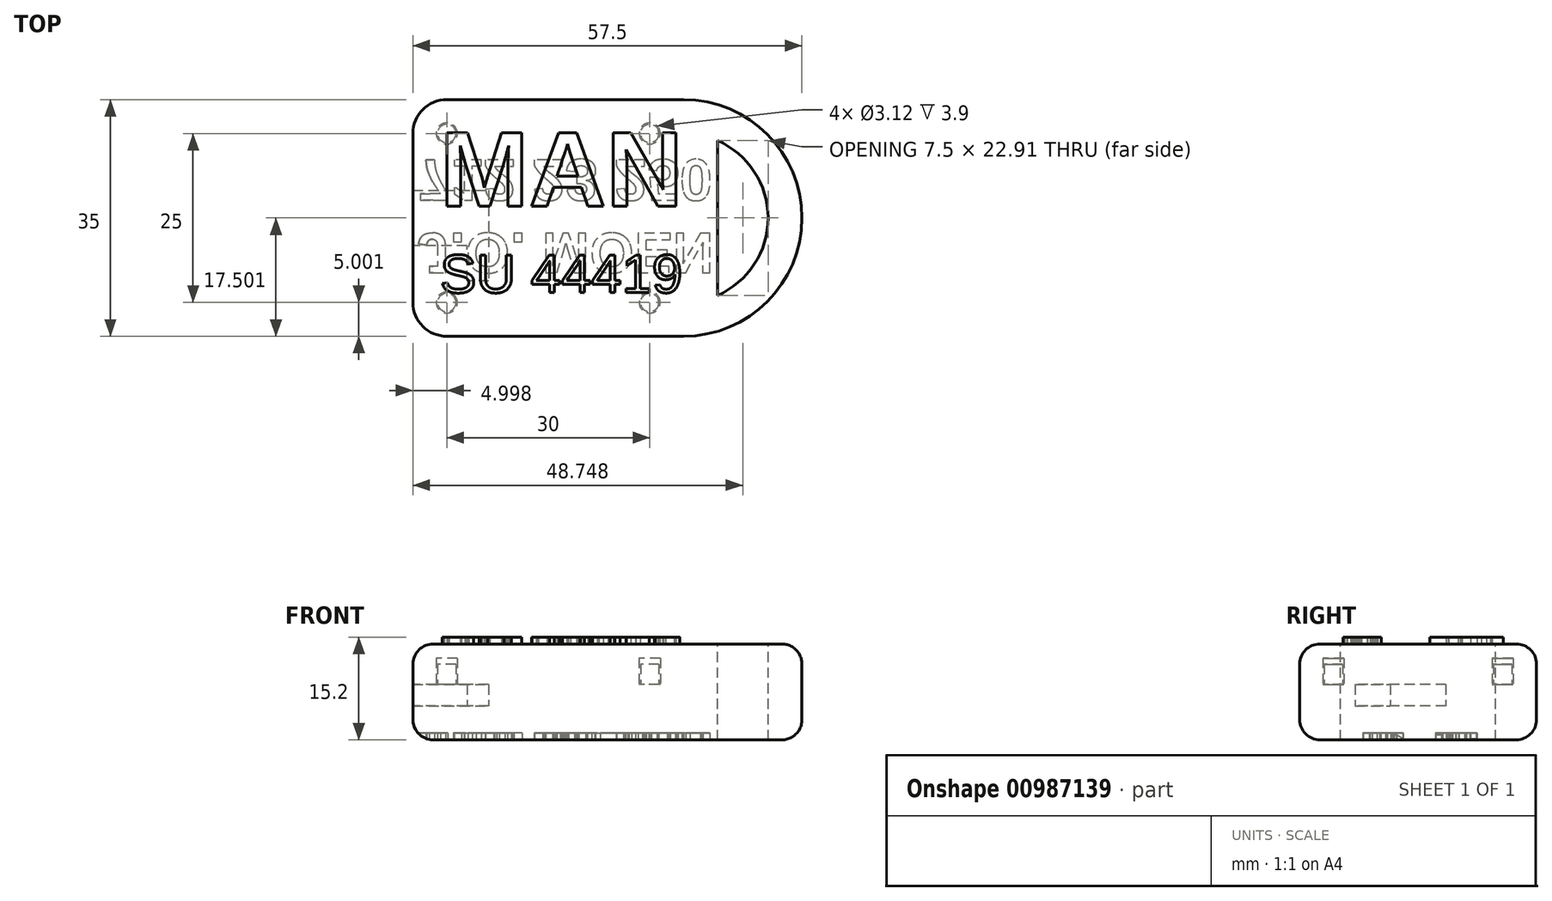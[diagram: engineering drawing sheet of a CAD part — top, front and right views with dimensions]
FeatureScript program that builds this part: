
annotation { "Feature Type Name" : "Feature", "Feature Type Description" : "" }
export const myFeature = defineFeature(function(context is Context, id is Id, definition is map)
    precondition{}
    {
        {
            var Q0;
            Q0=qCreatedBy(makeId("Top.planeOp"),FACE);
            var sketch = newSketch(context, id + "F0", { "sketchPlane" : qUnion([Q0])});
            skLineSegment(sketch, "E0.bottom", {"start": v(42.2, 28.64) * mm, "end": v(82.2, 28.64) * mm});
            skLineSegment(sketch, "E0.top", {"start": v(42.2, -6.36) * mm, "end": v(82.2, -6.36) * mm});
            skLineSegment(sketch, "E0.left", {"start": v(42.2, 28.64) * mm, "end": v(42.2, 15.24) * mm});
            skLineSegment(sketch, "E0.right", {"start": v(82.2, 28.64) * mm, "end": v(82.2, -6.36) * mm});
            skLineSegment(sketch, "E1", {"start": v(42.2, 7.04) * mm, "end": v(42.2, -6.36) * mm});
            skLineSegment(sketch, "E2", {"start": v(42.2, 15.24) * mm, "end": v(42.2, 7.04) * mm});
            skCircle(sketch, "E3", {"center": v(47.2, 23.64) * mm, "radius": 1.36 * mm});
            skLineSegment(sketch, "E4", {"start": v(47.2, 23.64) * mm, "end": v(47.2, 28.64) * mm, "construction": true});
            skLineSegment(sketch, "E5", {"start": v(47.2, 23.64) * mm, "end": v(42.2, 23.64) * mm, "construction": true});
            skCircle(sketch, "E6", {"center": v(47.2, -1.36) * mm, "radius": 1.36 * mm});
            skCircle(sketch, "E7", {"center": v(77.2, -1.36) * mm, "radius": 1.36 * mm});
            skCircle(sketch, "E8", {"center": v(77.2, 23.64) * mm, "radius": 1.36 * mm});
            skLineSegment(sketch, "E9", {"start": v(47.2, -1.36) * mm, "end": v(42.2, -1.36) * mm, "construction": true});
            skLineSegment(sketch, "E10", {"start": v(47.2, -1.36) * mm, "end": v(47.2, -6.36) * mm, "construction": true});
            skLineSegment(sketch, "E11", {"start": v(77.2, -1.36) * mm, "end": v(77.2, -6.36) * mm, "construction": true});
            skLineSegment(sketch, "E12", {"start": v(77.2, -1.36) * mm, "end": v(82.2, -1.36) * mm, "construction": true});
            skLineSegment(sketch, "E13", {"start": v(82.2, 23.64) * mm, "end": v(77.2, 23.64) * mm, "construction": true});
            skLineSegment(sketch, "E14", {"start": v(77.2, 23.64) * mm, "end": v(77.2, 28.64) * mm, "construction": true});
            skLineSegment(sketch, "E15", {"start": v(42.2, 15.24) * mm, "end": v(53.4, 15.24) * mm});
            skLineSegment(sketch, "E16", {"start": v(53.4, 15.24) * mm, "end": v(53.4, 7.04) * mm});
            skLineSegment(sketch, "E17", {"start": v(53.4, 7.04) * mm, "end": v(53.4, 1.84) * mm});
            skLineSegment(sketch, "E18", {"start": v(53.4, 1.84) * mm, "end": v(50.2, 1.84) * mm});
            skLineSegment(sketch, "E19", {"start": v(50.2, 1.84) * mm, "end": v(50.2, 7.04) * mm});
            skLineSegment(sketch, "E20", {"start": v(50.2, 7.04) * mm, "end": v(42.2, 7.04) * mm});
            skSolve(sketch);
        }
        {
            var Q0;
            {var subQ4=sQuery(id+"F0.wireOp",EDGE,"E0.bottom");Q0=makeQuery(id+"F0.imprint","IMPRINT",FACE,{"disambiguationData":[TD([[makeQuery(id+"F0.imprint","IMPRINT",EDGE,{"derivedFrom":subQ4}),-1.0]])]});}
            extrude(context, id + "F1", {"entities" : qUnion([Q0]), "depth" : 3.2 * mm, "offsetDistance" : 25 * mm});
        }
        {
            var Q0;
            {var subQ4=sQuery(id+"F0.wireOp",EDGE,"E0.bottom");Q0=makeQuery(id+"F0.imprint","IMPRINT",FACE,{"disambiguationData":[TD([[makeQuery(id+"F0.imprint","IMPRINT",EDGE,{"derivedFrom":subQ4}),-1.0]])]});}
            var Q1;
            {var subQ1=sQuery(id+"F0.wireOp",EDGE,"E2");Q1=makeQuery(id+"F0.imprint","IMPRINT",FACE,{"disambiguationData":[TD([[makeQuery(id+"F0.imprint","IMPRINT",EDGE,{"derivedFrom":subQ1}),1.0]])]});}
            var Q2;
            Q2=makeQuery(id+"F0.imprint","IMPRINT",FACE,{"disambiguationData":[TD([[makeQuery(id+"F0.imprint","IMPRINT",EDGE,{"derivedFrom":sQuery(id+"F0.wireOp",EDGE,"bb15f0e1-cc91-4aa7-aae3-7d4c7bcce2f1.0")}),1.0]])]});
            var Q3;
            Q3=makeQuery(id+"F0.imprint","IMPRINT",FACE,{"disambiguationData":[TD([[makeQuery(id+"F0.imprint","IMPRINT",EDGE,{"derivedFrom":sQuery(id+"F0.wireOp",EDGE,"E7")}),1.0]])]});
            var Q4;
            Q4=makeQuery(id+"F0.imprint","IMPRINT",FACE,{"disambiguationData":[TD([[makeQuery(id+"F0.imprint","IMPRINT",EDGE,{"derivedFrom":sQuery(id+"F0.wireOp",EDGE,"E3")}),1.0]])]});
            var Q5;
            Q5=makeQuery(id+"F0.imprint","IMPRINT",FACE,{"disambiguationData":[TD([[makeQuery(id+"F0.imprint","IMPRINT",EDGE,{"derivedFrom":sQuery(id+"F0.wireOp",EDGE,"E8")}),1.0]])]});
            var Q6;
            Q6=makeQuery(id+"F0.imprint","IMPRINT",FACE,{"disambiguationData":[TD([[makeQuery(id+"F0.imprint","IMPRINT",EDGE,{"derivedFrom":sQuery(id+"F0.wireOp",EDGE,"E6")}),1.0]])]});
            extrude(context, id + "F2", {"entities" : qUnion([Q0, Q1, Q2, Q3, Q4, Q5, Q6]), "operationType" : NewBodyOperationType.ADD, "oppositeDirection" : true, "depth" : 5 * mm, "offsetDistance" : 25 * mm});
        }
        {
            var Q0;
            Q0=makeQuery(id+"F0.imprint","IMPRINT",FACE,{"disambiguationData":[TD([[makeQuery(id+"F0.imprint","IMPRINT",EDGE,{"derivedFrom":sQuery(id+"F0.wireOp",EDGE,"E6")}),1.0]])]});
            var Q1;
            Q1=makeQuery(id+"F0.imprint","IMPRINT",FACE,{"disambiguationData":[TD([[makeQuery(id+"F0.imprint","IMPRINT",EDGE,{"derivedFrom":sQuery(id+"F0.wireOp",EDGE,"E7")}),1.0]])]});
            var Q2;
            Q2=makeQuery(id+"F0.imprint","IMPRINT",FACE,{"disambiguationData":[TD([[makeQuery(id+"F0.imprint","IMPRINT",EDGE,{"derivedFrom":sQuery(id+"F0.wireOp",EDGE,"E8")}),1.0]])]});
            var Q3;
            Q3=makeQuery(id+"F0.imprint","IMPRINT",FACE,{"disambiguationData":[TD([[makeQuery(id+"F0.imprint","IMPRINT",EDGE,{"derivedFrom":sQuery(id+"F0.wireOp",EDGE,"E3")}),1.0]])]});
            var Q4;
            Q4=makeQuery(id+"F1.opExtrude","CAP_FACE",FACE,{"disambiguationData":[OSD([sQuery(id+"F0.wireOp",EDGE,"E0.bottom"),sQuery(id+"F0.wireOp",EDGE,"E0.top"),sQuery(id+"F0.wireOp",EDGE,"E0.left"),sQuery(id+"F0.wireOp",EDGE,"E0.right"),sQuery(id+"F0.wireOp",EDGE,"E1"),sQuery(id+"F0.wireOp",EDGE,"fb78b1c1-1042-4b1b-a41c-8e915558833c.0"),sQuery(id+"F0.wireOp",EDGE,"fb78b1c1-1042-4b1b-a41c-8e915558833c.1"),sQuery(id+"F0.wireOp",EDGE,"fb78b1c1-1042-4b1b-a41c-8e915558833c.2"),sQuery(id+"F0.wireOp",EDGE,"fb78b1c1-1042-4b1b-a41c-8e915558833c.3"),sQuery(id+"F0.wireOp",EDGE,"fb78b1c1-1042-4b1b-a41c-8e915558833c.4"),sQuery(id+"F0.wireOp",EDGE,"fb78b1c1-1042-4b1b-a41c-8e915558833c.5"),sQuery(id+"F0.wireOp",EDGE,"fb78b1c1-1042-4b1b-a41c-8e915558833c.6"),sQuery(id+"F0.wireOp",EDGE,"fb78b1c1-1042-4b1b-a41c-8e915558833c.7"),sQuery(id+"F0.wireOp",EDGE,"fb78b1c1-1042-4b1b-a41c-8e915558833c.8"),sQuery(id+"F0.wireOp",EDGE,"fb78b1c1-1042-4b1b-a41c-8e915558833c.9"),sQuery(id+"F0.wireOp",EDGE,"fb78b1c1-1042-4b1b-a41c-8e915558833c.10"),sQuery(id+"F0.wireOp",EDGE,"E3"),sQuery(id+"F0.wireOp",EDGE,"E6"),sQuery(id+"F0.wireOp",EDGE,"E7"),sQuery(id+"F0.wireOp",EDGE,"E8")])],"isStart":false});
            extrude(context, id + "F3", {"entities" : qUnion([Q0, Q1, Q2, Q3]), "operationType" : NewBodyOperationType.ADD, "endBound" : BoundingType.UP_TO_SURFACE, "depth" : 5 * mm, "endBoundEntityFace" : qUnion([Q4]), "hasOffset" : true, "offsetDistance" : 3 * mm, "offsetOppositeDirection" : true});
        }
        {
            var Q0;
            Q0=makeQuery(id+"F1.opExtrude","CAP_FACE",FACE,{"disambiguationData":[OSD([sQuery(id+"F0.wireOp",EDGE,"E0.bottom"),sQuery(id+"F0.wireOp",EDGE,"E0.top"),sQuery(id+"F0.wireOp",EDGE,"E0.left"),sQuery(id+"F0.wireOp",EDGE,"E0.right"),sQuery(id+"F0.wireOp",EDGE,"E1"),sQuery(id+"F0.wireOp",EDGE,"fb78b1c1-1042-4b1b-a41c-8e915558833c.0"),sQuery(id+"F0.wireOp",EDGE,"fb78b1c1-1042-4b1b-a41c-8e915558833c.1"),sQuery(id+"F0.wireOp",EDGE,"fb78b1c1-1042-4b1b-a41c-8e915558833c.2"),sQuery(id+"F0.wireOp",EDGE,"fb78b1c1-1042-4b1b-a41c-8e915558833c.3"),sQuery(id+"F0.wireOp",EDGE,"fb78b1c1-1042-4b1b-a41c-8e915558833c.4"),sQuery(id+"F0.wireOp",EDGE,"fb78b1c1-1042-4b1b-a41c-8e915558833c.5"),sQuery(id+"F0.wireOp",EDGE,"fb78b1c1-1042-4b1b-a41c-8e915558833c.6"),sQuery(id+"F0.wireOp",EDGE,"fb78b1c1-1042-4b1b-a41c-8e915558833c.7"),sQuery(id+"F0.wireOp",EDGE,"fb78b1c1-1042-4b1b-a41c-8e915558833c.8"),sQuery(id+"F0.wireOp",EDGE,"fb78b1c1-1042-4b1b-a41c-8e915558833c.9"),sQuery(id+"F0.wireOp",EDGE,"fb78b1c1-1042-4b1b-a41c-8e915558833c.10"),sQuery(id+"F0.wireOp",EDGE,"E3"),sQuery(id+"F0.wireOp",EDGE,"E6"),sQuery(id+"F0.wireOp",EDGE,"E7"),sQuery(id+"F0.wireOp",EDGE,"E8")])],"isStart":false});
            var sketch = newSketch(context, id + "F4", { "sketchPlane" : qUnion([Q0])});
            skLineSegment(sketch, "E21.bottom", {"start": v(42.2, 28.64) * mm, "end": v(82.2, 28.64) * mm});
            skLineSegment(sketch, "E21.top", {"start": v(42.2, -6.36) * mm, "end": v(82.2, -6.36) * mm});
            skLineSegment(sketch, "E21.left", {"start": v(42.2, 28.64) * mm, "end": v(42.2, -6.36) * mm});
            skLineSegment(sketch, "E21.right", {"start": v(82.2, 28.64) * mm, "end": v(82.2, -6.36) * mm});
            skCircle(sketch, "E22", {"center": v(47.2, 23.64) * mm, "radius": 1.56 * mm});
            skCircle(sketch, "E23", {"center": v(77.2, 23.64) * mm, "radius": 1.56 * mm});
            skCircle(sketch, "E24", {"center": v(77.2, -1.36) * mm, "radius": 1.56 * mm});
            skCircle(sketch, "E25", {"center": v(47.2, -1.36) * mm, "radius": 1.56 * mm});
            skSolve(sketch);
        }
        {
            var Q0;
            {var subQ1=sQuery(id+"F4.wireOp",EDGE,"E21.bottom");Q0=makeQuery(id+"F4.imprint","IMPRINT",FACE,{"disambiguationData":[TD([[makeQuery(id+"F4.imprint","IMPRINT",EDGE,{"derivedFrom":subQ1}),-1.0]])]});}
            var Q1;
            {var subQ2=makeQuery(id+"F1.opExtrude","CAP_EDGE",EDGE,{"disambiguationData":[OSD([sQuery(id+"F0.wireOp",EDGE,"fb78b1c1-1042-4b1b-a41c-8e915558833c.0")])],"isStart":false});Q1=makeQuery(id+"F4.imprint","IMPRINT",FACE,{"disambiguationData":[TD([[makeQuery(id+"F4.imprint","IMPRINT",EDGE,{"derivedFrom":subQ2}),-1.0]])]});}
            var Q2;
            {var subQ0=makeQuery(id+"F1.opExtrude","CAP_EDGE",EDGE,{"disambiguationData":[OSD([sQuery(id+"F0.wireOp",EDGE,"E15")])],"isStart":false});Q2=makeQuery(id+"F4.imprint","IMPRINT",FACE,{"disambiguationData":[TD([[makeQuery(id+"F4.imprint","IMPRINT",EDGE,{"derivedFrom":subQ0}),-1.0]])]});}
            var Q3;
            Q3=makeQuery(id+"F3.opExtrude","CAP_FACE",FACE,{"disambiguationData":[OSD([sQuery(id+"F0.wireOp",EDGE,"E3")])],"isStart":false});
            extrude(context, id + "F5", {"entities" : qUnion([Q0, Q1, Q2]), "endBound" : BoundingType.UP_TO_SURFACE, "depth" : 25 * mm, "endBoundEntityFace" : qUnion([Q3]), "hasOffset" : true, "offsetDistance" : 1 * mm, "offsetOppositeDirection" : true});
        }
        {
            var Q0;
            Q0=makeQuery(id+"F5.opExtrude","CAP_FACE",FACE,{"disambiguationData":[OSD([sQuery(id+"F4.wireOp",EDGE,"E21.bottom"),sQuery(id+"F4.wireOp",EDGE,"E21.top"),sQuery(id+"F4.wireOp",EDGE,"E21.left"),sQuery(id+"F4.wireOp",EDGE,"E21.right"),sQuery(id+"F4.wireOp",EDGE,"E22"),sQuery(id+"F4.wireOp",EDGE,"E23"),sQuery(id+"F4.wireOp",EDGE,"E24"),sQuery(id+"F4.wireOp",EDGE,"E25")])],"isStart":false});
            var sketch = newSketch(context, id + "F6", { "sketchPlane" : qUnion([Q0])});
            skLineSegment(sketch, "E26.bottom", {"start": v(42.2, 28.64) * mm, "end": v(82.2, 28.64) * mm});
            skLineSegment(sketch, "E26.top", {"start": v(42.2, -6.36) * mm, "end": v(82.2, -6.36) * mm});
            skLineSegment(sketch, "E26.left", {"start": v(42.2, 28.64) * mm, "end": v(42.2, -6.36) * mm});
            skLineSegment(sketch, "E26.right", {"start": v(82.2, 28.64) * mm, "end": v(82.2, -6.36) * mm});
            skSolve(sketch);
        }
        {
            var Q0;
            Q0=makeQuery(id+"F6.imprint","IMPRINT",FACE,{"disambiguationData":[TD([[makeQuery(id+"F6.imprint","IMPRINT",EDGE,{"derivedFrom":makeQuery(id+"F5.opExtrude","CAP_EDGE",EDGE,{"disambiguationData":[OSD([sQuery(id+"F4.wireOp",EDGE,"E22")])],"isStart":false})}),1.0]])]});
            var Q1;
            Q1=makeQuery(id+"F6.imprint","IMPRINT",FACE,{"disambiguationData":[TD([[makeQuery(id+"F6.imprint","IMPRINT",EDGE,{"derivedFrom":makeQuery(id+"F5.opExtrude","CAP_EDGE",EDGE,{"disambiguationData":[OSD([sQuery(id+"F4.wireOp",EDGE,"E24")])],"isStart":false})}),1.0]])]});
            var Q2;
            Q2=makeQuery(id+"F6.imprint","IMPRINT",FACE,{"disambiguationData":[TD([[makeQuery(id+"F6.imprint","IMPRINT",EDGE,{"derivedFrom":makeQuery(id+"F5.opExtrude","CAP_EDGE",EDGE,{"disambiguationData":[OSD([sQuery(id+"F4.wireOp",EDGE,"E23")])],"isStart":false})}),1.0]])]});
            var Q3;
            Q3=makeQuery(id+"F6.imprint","IMPRINT",FACE,{"disambiguationData":[TD([[makeQuery(id+"F6.imprint","IMPRINT",EDGE,{"derivedFrom":makeQuery(id+"F5.opExtrude","CAP_EDGE",EDGE,{"disambiguationData":[OSD([sQuery(id+"F4.wireOp",EDGE,"E25")])],"isStart":false})}),1.0]])]});
            var Q4;
            Q4=makeQuery(id+"F3.opExtrude","CAP_FACE",FACE,{"disambiguationData":[OSD([sQuery(id+"F0.wireOp",EDGE,"E6")])],"isStart":false});
            extrude(context, id + "F7", {"entities" : qUnion([Q0, Q1, Q2, Q3]), "operationType" : NewBodyOperationType.ADD, "endBound" : BoundingType.UP_TO_SURFACE, "oppositeDirection" : true, "depth" : 25 * mm, "endBoundEntityFace" : qUnion([Q4]), "hasOffset" : true, "offsetDistance" : 0.9 * mm});
        }
        {
            var Q0;
            {var subQ0=sQuery(id+"F4.wireOp",EDGE,"E25");var subQ1=sQuery(id+"F4.wireOp",EDGE,"E24");var subQ2=sQuery(id+"F4.wireOp",EDGE,"E23");var subQ3=sQuery(id+"F4.wireOp",EDGE,"E22");Q0=makeQuery(id+"F7.boolean.opBoolean","MERGE",FACE,{"derivedFrom":[makeQuery(id+"F5.opExtrude","CAP_FACE",FACE,{"disambiguationData":[OSD([sQuery(id+"F4.wireOp",EDGE,"E21.bottom"),sQuery(id+"F4.wireOp",EDGE,"E21.top"),sQuery(id+"F4.wireOp",EDGE,"E21.left"),sQuery(id+"F4.wireOp",EDGE,"E21.right"),subQ3,subQ2,subQ1,subQ0])],"isStart":false}),makeQuery(id+"F7.opExtrude","CAP_FACE",FACE,{"disambiguationData":[OSD([subQ3])],"isStart":true}),makeQuery(id+"F7.opExtrude","CAP_FACE",FACE,{"disambiguationData":[OSD([subQ2])],"isStart":true}),makeQuery(id+"F7.opExtrude","CAP_FACE",FACE,{"disambiguationData":[OSD([subQ1])],"isStart":true}),makeQuery(id+"F7.opExtrude","CAP_FACE",FACE,{"disambiguationData":[OSD([subQ0])],"isStart":true})]});}
            var sketch = newSketch(context, id + "F8", { "sketchPlane" : qUnion([Q0])});
            skSolve(sketch);
        }
        {
            var Q0;
            Q0=makeQuery(id+"F8.imprint","IMPRINT",FACE,{"disambiguationData":[TD([[makeQuery(id+"F8.imprint","IMPRINT",EDGE,{"derivedFrom":makeQuery(id+"F5.opExtrude","CAP_EDGE",EDGE,{"disambiguationData":[OSD([sQuery(id+"F4.wireOp",EDGE,"E21.bottom")])],"isStart":false})}),-1.0]])]});
            extrude(context, id + "F9", {"entities" : qUnion([Q0]), "operationType" : NewBodyOperationType.ADD, "depth" : 2 * mm, "offsetDistance" : 25 * mm});
        }
        {
            var Q0;
            Q0=makeQuery(id+"F9.opExtrude","CAP_FACE",FACE,{"disambiguationData":[OSD([sQuery(id+"F4.wireOp",EDGE,"E21.bottom"),sQuery(id+"F4.wireOp",EDGE,"E21.top"),sQuery(id+"F4.wireOp",EDGE,"E21.left"),sQuery(id+"F4.wireOp",EDGE,"E21.right")])],"isStart":false});
            var sketch = newSketch(context, id + "F10", { "sketchPlane" : qUnion([Q0])});
            skText(sketch, "E27", { "text": "MAN", "fontName": "Arimo-Bold.ttf"});
            skText(sketch, "E28", { "text": "SU 44419", "fontName": "Arimo-Regular.ttf"});
            const initialGuessF10  = {"E27": [0.0462, 0.01287, 1, 0, 0.01137], "E28": [0.0462, 0.0001, 1, 0, 0.0058]};
            skSetInitialGuess(sketch, initialGuessF10);
            skSolve(sketch);
        }
        {
            var Q0;
            Q0 = qSketchRegion(id + "F10", true);
            extrude(context, id + "F11", {"entities" : qUnion([Q0]), "operationType" : NewBodyOperationType.ADD, "depth" : 1 * mm, "offsetDistance" : 25 * mm});
        }
        {
            var Q0;
            {var subQ0=sQuery(id+"F0.wireOp",EDGE,"E0.left");var subQ1=sQuery(id+"F0.wireOp",EDGE,"E0.bottom");Q0=makeQuery(id+"F2.boolean.opBoolean","MERGE",EDGE,{"derivedFrom":[makeQuery(id+"F1.opExtrude","SWEPT_EDGE",EDGE,{"disambiguationData":[OSD([subQ1,subQ0])]}),makeQuery(id+"F2.opExtrude","SWEPT_EDGE",EDGE,{"disambiguationData":[OSD([subQ1,subQ0])]})]});}
            var Q1;
            {var subQ0=sQuery(id+"F4.wireOp",EDGE,"E21.left");var subQ1=sQuery(id+"F4.wireOp",EDGE,"E21.bottom");Q1=makeQuery(id+"F9.boolean.opBoolean","MERGE",EDGE,{"derivedFrom":[makeQuery(id+"F5.opExtrude","SWEPT_EDGE",EDGE,{"disambiguationData":[OSD([subQ1,subQ0])]}),makeQuery(id+"F9.opExtrude","SWEPT_EDGE",EDGE,{"disambiguationData":[OSD([subQ1,subQ0])]})]});}
            var Q2;
            {var subQ0=sQuery(id+"F0.wireOp",EDGE,"E1");var subQ1=sQuery(id+"F0.wireOp",EDGE,"E0.top");Q2=makeQuery(id+"F2.boolean.opBoolean","MERGE",EDGE,{"derivedFrom":[makeQuery(id+"F1.opExtrude","SWEPT_EDGE",EDGE,{"disambiguationData":[OSD([subQ1,subQ0])]}),makeQuery(id+"F2.opExtrude","SWEPT_EDGE",EDGE,{"disambiguationData":[OSD([subQ1,subQ0])]})]});}
            var Q3;
            {var subQ0=sQuery(id+"F4.wireOp",EDGE,"E21.left");var subQ1=sQuery(id+"F4.wireOp",EDGE,"E21.top");Q3=makeQuery(id+"F9.boolean.opBoolean","MERGE",EDGE,{"derivedFrom":[makeQuery(id+"F5.opExtrude","SWEPT_EDGE",EDGE,{"disambiguationData":[OSD([subQ1,subQ0])]}),makeQuery(id+"F9.opExtrude","SWEPT_EDGE",EDGE,{"disambiguationData":[OSD([subQ1,subQ0])]})]});}
            fillet(context, id + "F12", {"entities" : qUnion([Q0, Q1, Q2, Q3]), "radius" : 5 * mm, "tangentPropagation" : true, "allowEdgeOverflow" : false});
        }
        {
            var Q0;
            {var subQ1=sQuery(id+"F4.wireOp",EDGE,"E21.right");var subQ3=sQuery(id+"F4.wireOp",EDGE,"E21.left");var subQ7=sQuery(id+"F4.wireOp",EDGE,"E21.bottom");var subQ12=sQuery(id+"F4.wireOp",EDGE,"E21.top");Q0=makeQuery(id+"F11.boolean.opBoolean","SPLIT",FACE,{"disambiguationData":[TD([makeQuery(id+"F5.opExtrude","SWEPT_FACE",FACE,{"disambiguationData":[OSD([subQ12])]})])],"derivedFrom":makeQuery(id+"F9.opExtrude","CAP_FACE",FACE,{"disambiguationData":[OSD([subQ7,subQ12,subQ3,subQ1])],"isStart":false})});}
            var sketch = newSketch(context, id + "F13", { "sketchPlane" : qUnion([Q0])});
            skArc(sketch, "E29", {"start": v(82.2, -6.36) * mm, "mid": v(99.7, 11.14) * mm, "end": v(82.2, 28.64) * mm});
            skArc(sketch, "E30.0", {"start": v(87.2, -0.32) * mm, "mid": v(94.7, 11.14) * mm, "end": v(87.2, 22.6) * mm});
            skLineSegment(sketch, "E30.1", {"start": v(87.2, 22.6) * mm, "end": v(87.2, -0.32) * mm});
            skSolve(sketch);
        }
        {
            var Q0;
            Q0=makeQuery(id+"F13.imprint","IMPRINT",FACE,{"disambiguationData":[TD([[makeQuery(id+"F13.imprint","IMPRINT",EDGE,{"derivedFrom":sQuery(id+"F13.wireOp",EDGE,"E29")}),1.0]])]});
            var Q1;
            Q1=makeQuery(id+"F5.opExtrude","CAP_FACE",FACE,{"disambiguationData":[OSD([sQuery(id+"F4.wireOp",EDGE,"E21.bottom"),sQuery(id+"F4.wireOp",EDGE,"E21.top"),sQuery(id+"F4.wireOp",EDGE,"E21.left"),sQuery(id+"F4.wireOp",EDGE,"E21.right"),sQuery(id+"F4.wireOp",EDGE,"E22"),sQuery(id+"F4.wireOp",EDGE,"E23"),sQuery(id+"F4.wireOp",EDGE,"E24"),sQuery(id+"F4.wireOp",EDGE,"E25")])],"isStart":true});
            extrude(context, id + "F14", {"entities" : qUnion([Q0]), "operationType" : NewBodyOperationType.ADD, "endBound" : BoundingType.UP_TO_SURFACE, "oppositeDirection" : true, "depth" : 25 * mm, "endBoundEntityFace" : qUnion([Q1]), "offsetDistance" : 25 * mm});
        }
        {
            var Q0;
            Q0=makeQuery(id+"F2.opExtrude","CAP_FACE",FACE,{"disambiguationData":[OSD([sQuery(id+"F0.wireOp",EDGE,"E0.bottom"),sQuery(id+"F0.wireOp",EDGE,"E0.top"),sQuery(id+"F0.wireOp",EDGE,"E0.left"),sQuery(id+"F0.wireOp",EDGE,"E0.right"),sQuery(id+"F0.wireOp",EDGE,"E1"),sQuery(id+"F0.wireOp",EDGE,"E2")])],"isStart":false});
            var sketch = newSketch(context, id + "F15", { "sketchPlane" : qUnion([Q0])});
            skArc(sketch, "E31", {"start": v(82.2, -28.64) * mm, "mid": v(99.7, -11.14) * mm, "end": v(82.2, 6.36) * mm});
            skArc(sketch, "E32.0", {"start": v(87.2, -22.6) * mm, "mid": v(94.7, -11.14) * mm, "end": v(87.2, 0.32) * mm});
            skLineSegment(sketch, "E32.1", {"start": v(87.2, -22.6) * mm, "end": v(87.2, 0.32) * mm});
            skSolve(sketch);
        }
        {
            var Q0;
            Q0=makeQuery(id+"F15.imprint","IMPRINT",FACE,{"disambiguationData":[TD([[makeQuery(id+"F15.imprint","IMPRINT",EDGE,{"derivedFrom":sQuery(id+"F15.wireOp",EDGE,"E31")}),1.0]])]});
            var Q1;
            Q1=makeQuery(id+"F1.opExtrude","CAP_FACE",FACE,{"disambiguationData":[OSD([sQuery(id+"F0.wireOp",EDGE,"E0.bottom"),sQuery(id+"F0.wireOp",EDGE,"E0.top"),sQuery(id+"F0.wireOp",EDGE,"E0.left"),sQuery(id+"F0.wireOp",EDGE,"E0.right"),sQuery(id+"F0.wireOp",EDGE,"E1"),sQuery(id+"F0.wireOp",EDGE,"E3"),sQuery(id+"F0.wireOp",EDGE,"E6"),sQuery(id+"F0.wireOp",EDGE,"E7"),sQuery(id+"F0.wireOp",EDGE,"E8"),sQuery(id+"F0.wireOp",EDGE,"E15"),sQuery(id+"F0.wireOp",EDGE,"E16"),sQuery(id+"F0.wireOp",EDGE,"E17"),sQuery(id+"F0.wireOp",EDGE,"E18"),sQuery(id+"F0.wireOp",EDGE,"E19"),sQuery(id+"F0.wireOp",EDGE,"E20")])],"isStart":false});
            extrude(context, id + "F16", {"entities" : qUnion([Q0]), "operationType" : NewBodyOperationType.ADD, "endBound" : BoundingType.UP_TO_SURFACE, "oppositeDirection" : true, "depth" : 25 * mm, "endBoundEntityFace" : qUnion([Q1]), "offsetDistance" : 25 * mm});
        }
        {
            var Q0;
            {var subQ0=sQuery(id+"F0.wireOp",EDGE,"E0.right");Q0=makeQuery(id+"F16.boolean.opBoolean","MERGE",FACE,{"derivedFrom":[makeQuery(id+"F2.opExtrude","CAP_FACE",FACE,{"disambiguationData":[OSD([sQuery(id+"F0.wireOp",EDGE,"E0.bottom"),sQuery(id+"F0.wireOp",EDGE,"E0.top"),sQuery(id+"F0.wireOp",EDGE,"E0.left"),subQ0,sQuery(id+"F0.wireOp",EDGE,"E1"),sQuery(id+"F0.wireOp",EDGE,"E2")])],"isStart":false}),makeQuery(id+"F16.opExtrude","CAP_FACE",FACE,{"disambiguationData":[OSD([subQ0,sQuery(id+"F15.wireOp",EDGE,"E31"),sQuery(id+"F15.wireOp",EDGE,"E32.0"),sQuery(id+"F15.wireOp",EDGE,"E32.1")])],"isStart":true})]});}
            var sketch = newSketch(context, id + "F17", { "sketchPlane" : qUnion([Q0])});
            skText(sketch, "E33", { "text": "J.O. MOEN", "fontName": "Arimo-Bold.ttf"});
            skText(sketch, "E34", { "text": "712 23 250", "fontName": "Arimo-Bold.ttf"});
            const initialGuessF17  = {"E33": [0.0429, -0.00887, 1, 0, 0.0061], "E34": [0.0429, -0.01976, 1, 0, 0.00627]};
            skSetInitialGuess(sketch, initialGuessF17);
            skSolve(sketch);
        }
        {
            var Q0;
            Q0 = qSketchRegion(id + "F17", true);
            var Q1;
            {var subQ0=sQuery(id+"F0.wireOp",EDGE,"E0.right");Q1=makeQuery(id+"F16.boolean.opBoolean","MERGE",FACE,{"derivedFrom":[makeQuery(id+"F2.opExtrude","CAP_FACE",FACE,{"disambiguationData":[OSD([sQuery(id+"F0.wireOp",EDGE,"E0.bottom"),sQuery(id+"F0.wireOp",EDGE,"E0.top"),sQuery(id+"F0.wireOp",EDGE,"E0.left"),subQ0,sQuery(id+"F0.wireOp",EDGE,"E1"),sQuery(id+"F0.wireOp",EDGE,"E2")])],"isStart":false}),makeQuery(id+"F16.opExtrude","CAP_FACE",FACE,{"disambiguationData":[OSD([subQ0,sQuery(id+"F15.wireOp",EDGE,"E31"),sQuery(id+"F15.wireOp",EDGE,"E32.0"),sQuery(id+"F15.wireOp",EDGE,"E32.1")])],"isStart":true})]});}
            extrude(context, id + "F18", {"entities" : qUnion([Q0]), "operationType" : NewBodyOperationType.REMOVE, "oppositeDirection" : true, "depth" : 1 * mm, "endBoundEntityFace" : qUnion([Q1]), "hasOffset" : true, "offsetDistance" : 1 * mm});
        }
        {
            var Q0;
            Q0=makeQuery(id+"F9.opExtrude","CAP_EDGE",EDGE,{"disambiguationData":[OSD([sQuery(id+"F4.wireOp",EDGE,"E21.left")])],"isStart":false});
            var Q1;
            {var subQ0=sQuery(id+"F4.wireOp",EDGE,"E21.right");var subQ1=sQuery(id+"F4.wireOp",EDGE,"E21.left");var subQ2=sQuery(id+"F4.wireOp",EDGE,"E21.top");var subQ3=sQuery(id+"F4.wireOp",EDGE,"E21.bottom");Q1=makeQuery(id+"F12.opFillet","BLEND_EDGE",EDGE,{"blendedFrom":[makeQuery(id+"F9.boolean.opBoolean","MERGE",EDGE,{"derivedFrom":[makeQuery(id+"F5.opExtrude","SWEPT_EDGE",EDGE,{"disambiguationData":[OSD([subQ2,subQ1])]}),makeQuery(id+"F9.opExtrude","SWEPT_EDGE",EDGE,{"disambiguationData":[OSD([subQ2,subQ1])]})]}),makeQuery(id+"F11.boolean.opBoolean","SPLIT",FACE,{"disambiguationData":[TD([makeQuery(id+"F5.opExtrude","SWEPT_FACE",FACE,{"disambiguationData":[OSD([subQ3])]})])],"derivedFrom":makeQuery(id+"F9.opExtrude","CAP_FACE",FACE,{"disambiguationData":[OSD([subQ3,subQ2,subQ1,subQ0])],"isStart":false})})],"blendedInto":[makeQuery(id+"F11.boolean.opBoolean","SPLIT",FACE,{"disambiguationData":[TD([makeQuery(id+"F5.opExtrude","SWEPT_FACE",FACE,{"disambiguationData":[OSD([subQ3])]})])],"derivedFrom":makeQuery(id+"F9.opExtrude","CAP_FACE",FACE,{"disambiguationData":[OSD([subQ3,subQ2,subQ1,subQ0])],"isStart":false})})]});}
            var Q2;
            Q2=makeQuery(id+"F9.opExtrude","CAP_EDGE",EDGE,{"disambiguationData":[OSD([sQuery(id+"F4.wireOp",EDGE,"E21.top")])],"isStart":false});
            var Q3;
            Q3=makeQuery(id+"F14.opExtrude","CAP_EDGE",EDGE,{"disambiguationData":[OSD([sQuery(id+"F13.wireOp",EDGE,"E29")])],"isStart":true});
            var Q4;
            Q4=makeQuery(id+"F9.opExtrude","CAP_EDGE",EDGE,{"disambiguationData":[OSD([sQuery(id+"F4.wireOp",EDGE,"E21.bottom")])],"isStart":false});
            var Q5;
            {var subQ0=sQuery(id+"F4.wireOp",EDGE,"E21.right");var subQ1=sQuery(id+"F4.wireOp",EDGE,"E21.left");var subQ2=sQuery(id+"F4.wireOp",EDGE,"E21.top");var subQ3=sQuery(id+"F4.wireOp",EDGE,"E21.bottom");Q5=makeQuery(id+"F12.opFillet","BLEND_EDGE",EDGE,{"blendedFrom":[makeQuery(id+"F9.boolean.opBoolean","MERGE",EDGE,{"derivedFrom":[makeQuery(id+"F5.opExtrude","SWEPT_EDGE",EDGE,{"disambiguationData":[OSD([subQ3,subQ1])]}),makeQuery(id+"F9.opExtrude","SWEPT_EDGE",EDGE,{"disambiguationData":[OSD([subQ3,subQ1])]})]}),makeQuery(id+"F11.boolean.opBoolean","SPLIT",FACE,{"disambiguationData":[TD([makeQuery(id+"F5.opExtrude","SWEPT_FACE",FACE,{"disambiguationData":[OSD([subQ3])]})])],"derivedFrom":makeQuery(id+"F9.opExtrude","CAP_FACE",FACE,{"disambiguationData":[OSD([subQ3,subQ2,subQ1,subQ0])],"isStart":false})})],"blendedInto":[makeQuery(id+"F11.boolean.opBoolean","SPLIT",FACE,{"disambiguationData":[TD([makeQuery(id+"F5.opExtrude","SWEPT_FACE",FACE,{"disambiguationData":[OSD([subQ3])]})])],"derivedFrom":makeQuery(id+"F9.opExtrude","CAP_FACE",FACE,{"disambiguationData":[OSD([subQ3,subQ2,subQ1,subQ0])],"isStart":false})})]});}
            var Q6;
            Q6=makeQuery(id+"F2.opExtrude","CAP_EDGE",EDGE,{"disambiguationData":[OSD([sQuery(id+"F0.wireOp",EDGE,"E0.left"),sQuery(id+"F0.wireOp",EDGE,"E1"),sQuery(id+"F0.wireOp",EDGE,"E2")])],"isStart":false});
            var Q7;
            {var subQ0=sQuery(id+"F0.wireOp",EDGE,"E1");var subQ1=sQuery(id+"F0.wireOp",EDGE,"E0.top");Q7=makeQuery(id+"F12.opFillet","BLEND_EDGE",EDGE,{"blendedFrom":[makeQuery(id+"F2.boolean.opBoolean","MERGE",EDGE,{"derivedFrom":[makeQuery(id+"F1.opExtrude","SWEPT_EDGE",EDGE,{"disambiguationData":[OSD([subQ1,subQ0])]}),makeQuery(id+"F2.opExtrude","SWEPT_EDGE",EDGE,{"disambiguationData":[OSD([subQ1,subQ0])]})]}),makeQuery(id+"F2.opExtrude","CAP_FACE",FACE,{"disambiguationData":[OSD([sQuery(id+"F0.wireOp",EDGE,"E0.bottom"),subQ1,sQuery(id+"F0.wireOp",EDGE,"E0.left"),sQuery(id+"F0.wireOp",EDGE,"E0.right"),subQ0,sQuery(id+"F0.wireOp",EDGE,"E2")])],"isStart":false})],"blendedInto":[makeQuery(id+"F2.opExtrude","CAP_FACE",FACE,{"disambiguationData":[OSD([sQuery(id+"F0.wireOp",EDGE,"E0.bottom"),subQ1,sQuery(id+"F0.wireOp",EDGE,"E0.left"),sQuery(id+"F0.wireOp",EDGE,"E0.right"),subQ0,sQuery(id+"F0.wireOp",EDGE,"E2")])],"isStart":false})]});}
            var Q8;
            Q8=makeQuery(id+"F2.opExtrude","CAP_EDGE",EDGE,{"disambiguationData":[OSD([sQuery(id+"F0.wireOp",EDGE,"E0.top")])],"isStart":false});
            var Q9;
            Q9=makeQuery(id+"F16.opExtrude","CAP_EDGE",EDGE,{"disambiguationData":[OSD([sQuery(id+"F15.wireOp",EDGE,"E31")])],"isStart":true});
            var Q10;
            Q10=makeQuery(id+"F2.opExtrude","CAP_EDGE",EDGE,{"disambiguationData":[OSD([sQuery(id+"F0.wireOp",EDGE,"E0.bottom")])],"isStart":false});
            var Q11;
            {var subQ0=sQuery(id+"F0.wireOp",EDGE,"E0.left");var subQ1=sQuery(id+"F0.wireOp",EDGE,"E0.bottom");Q11=makeQuery(id+"F12.opFillet","BLEND_EDGE",EDGE,{"blendedFrom":[makeQuery(id+"F2.boolean.opBoolean","MERGE",EDGE,{"derivedFrom":[makeQuery(id+"F1.opExtrude","SWEPT_EDGE",EDGE,{"disambiguationData":[OSD([subQ1,subQ0])]}),makeQuery(id+"F2.opExtrude","SWEPT_EDGE",EDGE,{"disambiguationData":[OSD([subQ1,subQ0])]})]}),makeQuery(id+"F2.opExtrude","CAP_FACE",FACE,{"disambiguationData":[OSD([subQ1,sQuery(id+"F0.wireOp",EDGE,"E0.top"),subQ0,sQuery(id+"F0.wireOp",EDGE,"E0.right"),sQuery(id+"F0.wireOp",EDGE,"E1"),sQuery(id+"F0.wireOp",EDGE,"E2")])],"isStart":false})],"blendedInto":[makeQuery(id+"F2.opExtrude","CAP_FACE",FACE,{"disambiguationData":[OSD([subQ1,sQuery(id+"F0.wireOp",EDGE,"E0.top"),subQ0,sQuery(id+"F0.wireOp",EDGE,"E0.right"),sQuery(id+"F0.wireOp",EDGE,"E1"),sQuery(id+"F0.wireOp",EDGE,"E2")])],"isStart":false})]});}
            fillet(context, id + "F19", {"entities" : qUnion([Q0, Q1, Q2, Q3, Q4, Q5, Q6, Q7, Q8, Q9, Q10, Q11]), "radius" : 3 * mm, "tangentPropagation" : true, "allowEdgeOverflow" : false});
        }
    });
